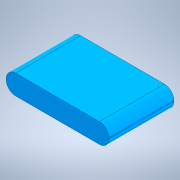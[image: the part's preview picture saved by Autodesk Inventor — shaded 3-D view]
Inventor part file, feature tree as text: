
AUTODESK INVENTOR PART (.ipt)
format: ipt  version: 2020.4 (Build 244396000, 396)  size: 107,520 bytes
history: native  units: mm
features: extrude x1, fillet x1, sketch x1
ambient origin geometry x8: Origin, YZ Plane, XZ Plane, XY Plane, X Axis, Y Axis, Z Axis, Center Point
bodies: Solid1 (feature_tree)
feature tree (3):
  extrude  "Extrusion1"  Depth=69.0mm
  fillet  "Fillet1"  Radius=21.0mm
  sketch  "Sketch1"  dims[d0=109.0mm d1=69.0mm d2=21.0mm d3=0.0mm d4=10.0mm]
